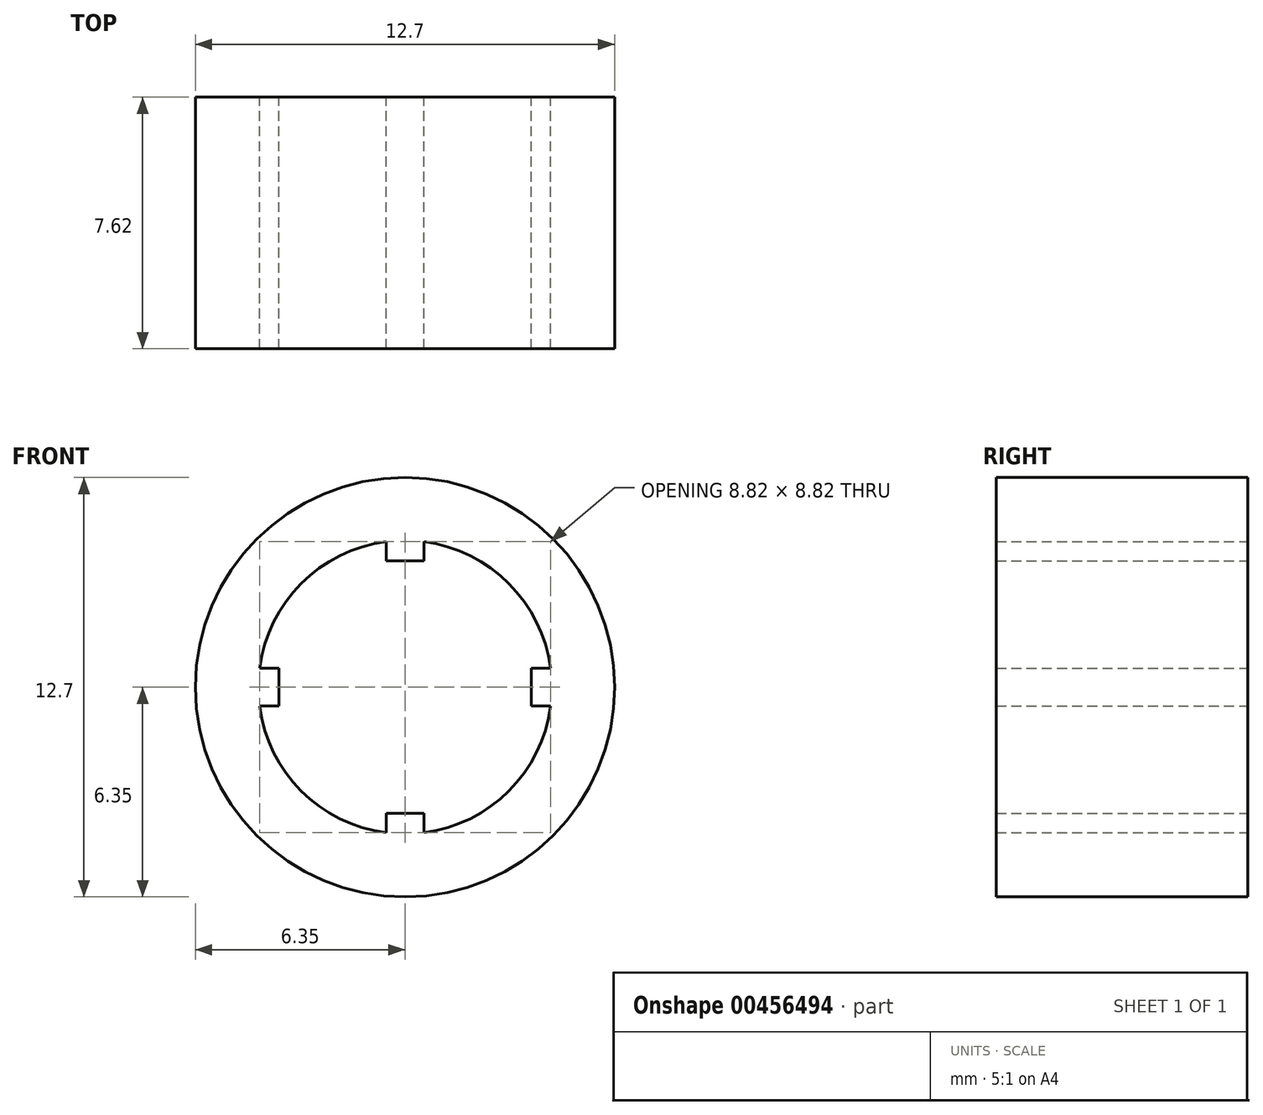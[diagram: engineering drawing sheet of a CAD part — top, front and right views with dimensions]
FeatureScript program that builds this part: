
annotation { "Feature Type Name" : "Feature", "Feature Type Description" : "" }
export const myFeature = defineFeature(function(context is Context, id is Id, definition is map)
    precondition{}
    {
        {
            var Q0;
            Q0=qCreatedBy(makeId("Front.planeOp"),FACE);
            var sketch = newSketch(context, id + "F0", { "sketchPlane" : qUnion([Q0])});
            skCircle(sketch, "E0", {"center": v(0, 0) * mm, "radius": 4.45 * mm});
            skCircle(sketch, "E1", {"center": v(0, 0) * mm, "radius": 6.35 * mm});
            skLineSegment(sketch, "E2", {"start": v(-0.57, 4.4) * mm, "end": v(-0.57, 3.82) * mm});
            skLineSegment(sketch, "E3", {"start": v(-0.57, 3.82) * mm, "end": v(0.57, 3.82) * mm});
            skLineSegment(sketch, "E4", {"start": v(0.57, 3.82) * mm, "end": v(0.57, 4.4) * mm});
            skLineSegment(sketch, "E5", {"start": v(-0.57, -4.4) * mm, "end": v(-0.57, -3.82) * mm});
            skLineSegment(sketch, "E6", {"start": v(-0.57, -3.82) * mm, "end": v(0.57, -3.82) * mm});
            skLineSegment(sketch, "E7", {"start": v(0.57, -3.82) * mm, "end": v(0.57, -4.4) * mm});
            skLineSegment(sketch, "E8", {"start": v(-4.4, 0.57) * mm, "end": v(-3.82, 0.57) * mm});
            skLineSegment(sketch, "E9", {"start": v(-3.82, 0.57) * mm, "end": v(-3.82, -0.57) * mm});
            skLineSegment(sketch, "E10", {"start": v(-3.82, -0.57) * mm, "end": v(-4.4, -0.57) * mm});
            skLineSegment(sketch, "E11", {"start": v(4.4, 0.57) * mm, "end": v(3.82, 0.57) * mm});
            skLineSegment(sketch, "E12", {"start": v(3.82, 0.57) * mm, "end": v(3.82, -0.57) * mm});
            skLineSegment(sketch, "E13", {"start": v(3.82, -0.57) * mm, "end": v(4.4, -0.57) * mm});
            skSolve(sketch);
        }
        {
            var Q0;
            Q0 = qSketchRegion(id + "F0", true);
            var Q1;
            {var subQ0=sQuery(id+"F0.wireOp",EDGE,"E2");Q1=makeQuery(id+"F0.imprint","IMPRINT",FACE,{"disambiguationData":[TD([[makeQuery(id+"F0.imprint","IMPRINT",EDGE,{"derivedFrom":subQ0}),1.0]])]});}
            var Q2;
            {var subQ0=sQuery(id+"F0.wireOp",EDGE,"E11");Q2=makeQuery(id+"F0.imprint","IMPRINT",FACE,{"disambiguationData":[TD([[makeQuery(id+"F0.imprint","IMPRINT",EDGE,{"derivedFrom":subQ0}),1.0]])]});}
            var Q3;
            {var subQ0=sQuery(id+"F0.wireOp",EDGE,"E5");Q3=makeQuery(id+"F0.imprint","IMPRINT",FACE,{"disambiguationData":[TD([[makeQuery(id+"F0.imprint","IMPRINT",EDGE,{"derivedFrom":subQ0}),-1.0]])]});}
            var Q4;
            {var subQ0=sQuery(id+"F0.wireOp",EDGE,"E8");Q4=makeQuery(id+"F0.imprint","IMPRINT",FACE,{"disambiguationData":[TD([[makeQuery(id+"F0.imprint","IMPRINT",EDGE,{"derivedFrom":subQ0}),-1.0]])]});}
            extrude(context, id + "F1", {"entities" : qUnion([Q0, Q1, Q2, Q3, Q4]), "depth" : 7.62 * mm, "offsetDistance" : 25.4 * mm});
        }
    });
